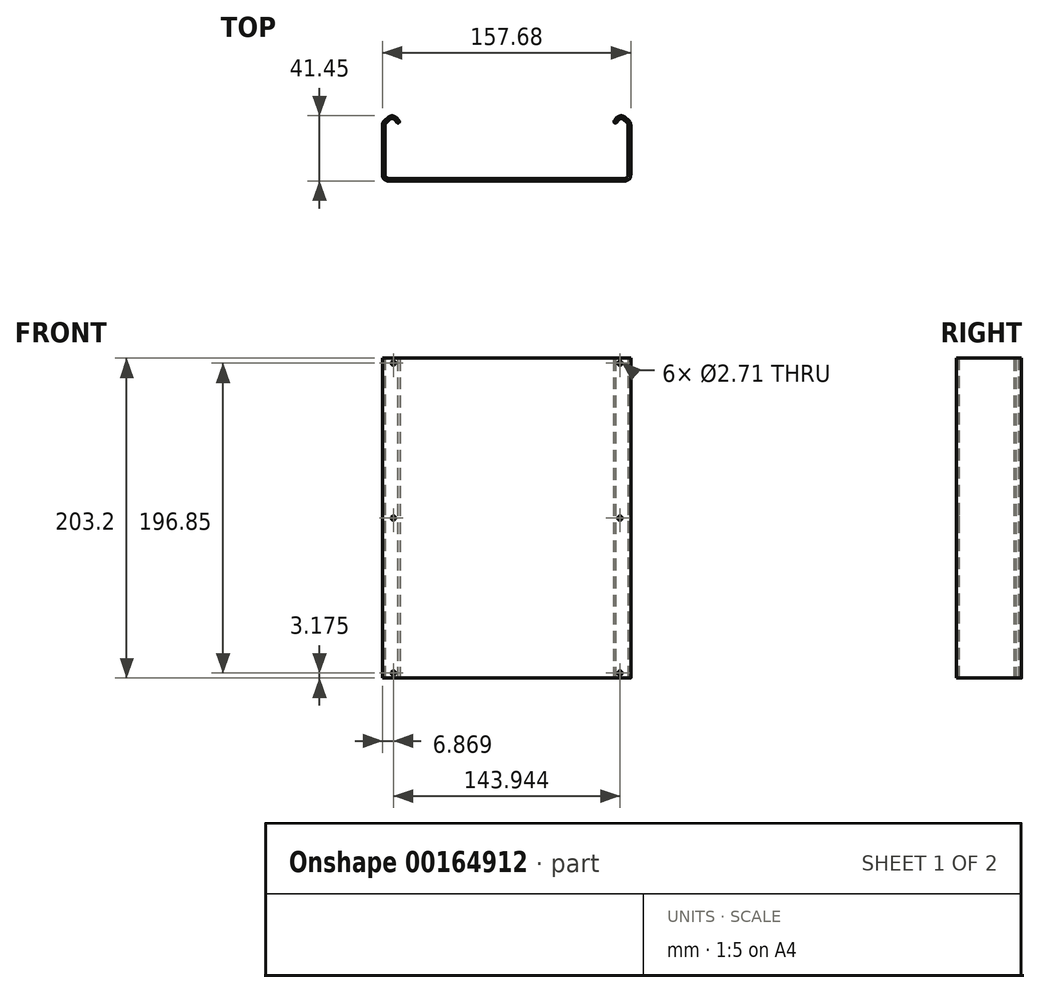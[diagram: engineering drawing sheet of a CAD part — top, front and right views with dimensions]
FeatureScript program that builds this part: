
annotation { "Feature Type Name" : "Feature", "Feature Type Description" : "" }
export const myFeature = defineFeature(function(context is Context, id is Id, definition is map)
    precondition{}
    {
        {
            var Q0;
            Q0=qCreatedBy(makeId("Top.planeOp"),FACE);
            var sketch = newSketch(context, id + "F0", { "sketchPlane" : qUnion([Q0])});
            skLineSegment(sketch, "E0", {"start": v(0, 0) * mm, "end": v(4.63, 3.93) * mm});
            skLineSegment(sketch, "E1", {"start": v(4.63, 3.93) * mm, "end": v(7.97, 0) * mm});
            skLineSegment(sketch, "E2", {"start": v(7.97, 0) * mm, "end": v(9.27, 1.1) * mm});
            skLineSegment(sketch, "E3", {"start": v(9.27, 1.1) * mm, "end": v(4.83, 6.34) * mm});
            skLineSegment(sketch, "E4", {"start": v(4.83, 6.34) * mm, "end": v(-1.7, 0.8) * mm});
            skLineSegment(sketch, "E5", {"start": v(0, 0) * mm, "end": v(0, -34.91) * mm});
            skLineSegment(sketch, "E6", {"start": v(0, -34.91) * mm, "end": v(154.26, -34.91) * mm});
            skLineSegment(sketch, "E7", {"start": v(155.97, -36.62) * mm, "end": v(-1.7, -36.62) * mm});
            skLineSegment(sketch, "E8", {"start": v(-1.7, -36.62) * mm, "end": v(-1.7, 0.8) * mm});
            skLineSegment(sketch, "E9", {"start": v(2.32, 1.97) * mm, "end": v(1.21, 3.27) * mm, "construction": true});
            skLineSegment(sketch, "E10", {"start": v(0, -34.91) * mm, "end": v(-1.7, -34.91) * mm, "construction": true});
            skLineSegment(sketch, "E11", {"start": v(77.13, -36.62) * mm, "end": v(77.13, -34.91) * mm, "construction": true});
            skLineSegment(sketch, "E12", {"start": v(154.26, -34.91) * mm, "end": v(154.26, 0) * mm});
            skLineSegment(sketch, "E13", {"start": v(154.26, 0) * mm, "end": v(149.63, 3.93) * mm});
            skLineSegment(sketch, "E14", {"start": v(149.63, 3.93) * mm, "end": v(146.29, 0) * mm});
            skLineSegment(sketch, "E15", {"start": v(146.29, 0) * mm, "end": v(144.99, 1.1) * mm});
            skLineSegment(sketch, "E16", {"start": v(144.99, 1.1) * mm, "end": v(149.43, 6.34) * mm});
            skLineSegment(sketch, "E17", {"start": v(149.43, 6.34) * mm, "end": v(155.97, 0.8) * mm});
            skLineSegment(sketch, "E18", {"start": v(155.97, 0.8) * mm, "end": v(155.97, -36.62) * mm});
            skArc(sketch, "E19", {"start": v(7.22, 3.53) * mm, "mid": v(4.7, 4.82) * mm, "end": v(2.01, 3.95) * mm, "construction": true});
            skArc(sketch, "E20", {"start": v(-0.4, 1.9) * mm, "mid": v(-1.37, 0.63) * mm, "end": v(-1.7, -0.92) * mm, "construction": true});
            skLineSegment(sketch, "E21", {"start": v(4.83, 6.34) * mm, "end": v(149.43, 6.34) * mm, "construction": true});
            skSolve(sketch);
        }
        {
            var Q0;
            Q0=qSketchRegion(id+"F0",true);
            extrude(context, id + "F1", {"entities" : qUnion([Q0]), "depth" : 203.2 * mm});
        }
        {
            var Q0;
            Q0=makeQuery(id+"F1.opExtrude","SWEPT_EDGE",EDGE,{"disambiguationData":[OSD([sQuery(id+"F0.wireOp",EDGE,"E16"),sQuery(id+"F0.wireOp",EDGE,"E17")])]});
            var Q1;
            Q1=makeQuery(id+"F1.opExtrude","SWEPT_EDGE",EDGE,{"disambiguationData":[OSD([sQuery(id+"F0.wireOp",EDGE,"E17"),sQuery(id+"F0.wireOp",EDGE,"E18")])]});
            var Q2;
            Q2=makeQuery(id+"F1.opExtrude","SWEPT_EDGE",EDGE,{"disambiguationData":[OSD([sQuery(id+"F0.wireOp",EDGE,"E7"),sQuery(id+"F0.wireOp",EDGE,"E18")])]});
            var Q3;
            Q3=makeQuery(id+"F1.opExtrude","SWEPT_EDGE",EDGE,{"disambiguationData":[OSD([sQuery(id+"F0.wireOp",EDGE,"E7"),sQuery(id+"F0.wireOp",EDGE,"E8")])]});
            var Q4;
            Q4=makeQuery(id+"F1.opExtrude","SWEPT_EDGE",EDGE,{"disambiguationData":[OSD([sQuery(id+"F0.wireOp",EDGE,"E4"),sQuery(id+"F0.wireOp",EDGE,"E8")])]});
            var Q5;
            Q5=makeQuery(id+"F1.opExtrude","SWEPT_EDGE",EDGE,{"disambiguationData":[OSD([sQuery(id+"F0.wireOp",EDGE,"E3"),sQuery(id+"F0.wireOp",EDGE,"E4")])]});
            fillet(context, id + "F2", {"entities" : qUnion([Q0, Q1, Q2, Q3, Q4, Q5]), "radius" : 3.7 * mm, "tangentPropagation" : true, "allowEdgeOverflow" : false});
        }
        {
            var Q0;
            Q0=makeQuery(id+"F1.opExtrude","SWEPT_EDGE",EDGE,{"disambiguationData":[OSD([sQuery(id+"F0.wireOp",EDGE,"E13"),sQuery(id+"F0.wireOp",EDGE,"E14")])]});
            var Q1;
            Q1=makeQuery(id+"F1.opExtrude","SWEPT_EDGE",EDGE,{"disambiguationData":[OSD([sQuery(id+"F0.wireOp",EDGE,"E12"),sQuery(id+"F0.wireOp",EDGE,"E13")])]});
            var Q2;
            Q2=makeQuery(id+"F1.opExtrude","SWEPT_EDGE",EDGE,{"disambiguationData":[OSD([sQuery(id+"F0.wireOp",EDGE,"E6"),sQuery(id+"F0.wireOp",EDGE,"E12")])]});
            var Q3;
            Q3=makeQuery(id+"F1.opExtrude","SWEPT_EDGE",EDGE,{"disambiguationData":[OSD([sQuery(id+"F0.wireOp",EDGE,"E5"),sQuery(id+"F0.wireOp",EDGE,"E6")])]});
            var Q4;
            Q4=makeQuery(id+"F1.opExtrude","SWEPT_EDGE",EDGE,{"disambiguationData":[OSD([sQuery(id+"F0.wireOp",EDGE,"E0"),sQuery(id+"F0.wireOp",EDGE,"E5")])]});
            var Q5;
            Q5=makeQuery(id+"F1.opExtrude","SWEPT_EDGE",EDGE,{"disambiguationData":[OSD([sQuery(id+"F0.wireOp",EDGE,"E0"),sQuery(id+"F0.wireOp",EDGE,"E1")])]});
            fillet(context, id + "F3", {"entities" : qUnion([Q0, Q1, Q2, Q3, Q4, Q5]), "radius" : 1.98 * mm, "tangentPropagation" : true, "allowEdgeOverflow" : false});
        }
        {
            var Q0;
            Q0=makeQuery(id+"F1.opExtrude","CAP_EDGE",EDGE,{"disambiguationData":[OSD([sQuery(id+"F0.wireOp",EDGE,"E15")])],"isStart":false});
            var Q1;
            Q1=makeQuery(id+"F1.opExtrude","CAP_EDGE",EDGE,{"disambiguationData":[OSD([sQuery(id+"F0.wireOp",EDGE,"E15")])],"isStart":true});
            var Q2;
            Q2=makeQuery(id+"F1.opExtrude","CAP_EDGE",EDGE,{"disambiguationData":[OSD([sQuery(id+"F0.wireOp",EDGE,"E2")])],"isStart":true});
            var Q3;
            Q3=makeQuery(id+"F1.opExtrude","CAP_EDGE",EDGE,{"disambiguationData":[OSD([sQuery(id+"F0.wireOp",EDGE,"E2")])],"isStart":false});
            fillet(context, id + "F4", {"entities" : qUnion([Q0, Q1, Q2, Q3]), "radius" : 0.76 * mm, "tangentPropagation" : true, "allowEdgeOverflow" : false});
        }
        {
            var Q0;
            Q0=makeQuery(id+"F1.opExtrude","SWEPT_FACE",FACE,{"disambiguationData":[OSD([sQuery(id+"F0.wireOp",EDGE,"E6")])]});
            var sketch = newSketch(context, id + "F5", { "sketchPlane" : qUnion([Q0])});
            skLineSegment(sketch, "E22.bottom", {"start": v(-1.98, 0) * mm, "end": v(-5.16, 0) * mm, "construction": true});
            skLineSegment(sketch, "E22.top", {"start": v(-1.98, 3.17) * mm, "end": v(-5.16, 3.17) * mm, "construction": true});
            skLineSegment(sketch, "E22.left", {"start": v(-1.98, 0) * mm, "end": v(-1.98, 3.17) * mm, "construction": true});
            skLineSegment(sketch, "E22.right", {"start": v(-5.16, 0) * mm, "end": v(-5.16, 3.18) * mm, "construction": true});
            skLineSegment(sketch, "E23", {"start": v(-77.13, 0) * mm, "end": v(-77.13, 203.2) * mm, "construction": true});
            skLineSegment(sketch, "E24.bottom", {"start": v(-5.16, 3.17) * mm, "end": v(-149.1, 3.17) * mm, "construction": true});
            skLineSegment(sketch, "E24.top", {"start": v(-5.16, 200.03) * mm, "end": v(-149.1, 200.03) * mm, "construction": true});
            skLineSegment(sketch, "E24.left", {"start": v(-5.16, 3.17) * mm, "end": v(-5.16, 200.03) * mm, "construction": true});
            skLineSegment(sketch, "E24.right", {"start": v(-149.1, 3.17) * mm, "end": v(-149.1, 200.03) * mm, "construction": true});
            skPoint(sketch, "E24.middle", {"position": v(-77.13, 101.6) * mm});
            skCircle(sketch, "E25", {"center": v(-5.16, 3.17) * mm, "radius": 1.35 * mm});
            skCircle(sketch, "E26", {"center": v(-5.16, 101.6) * mm, "radius": 1.35 * mm});
            skCircle(sketch, "E27", {"center": v(-5.16, 200.03) * mm, "radius": 1.35 * mm});
            skCircle(sketch, "E28", {"center": v(-149.1, 200.03) * mm, "radius": 1.35 * mm});
            skCircle(sketch, "E29", {"center": v(-149.1, 101.6) * mm, "radius": 1.35 * mm});
            skCircle(sketch, "E30", {"center": v(-149.1, 3.17) * mm, "radius": 1.35 * mm});
            skSolve(sketch);
        }
        {
            var Q0;
            Q0 = qSketchRegion(id + "F5", true);
            var Q1;
            Q1=makeQuery(id+"F1.opExtrude","SWEPT_FACE",FACE,{"disambiguationData":[OSD([sQuery(id+"F0.wireOp",EDGE,"E7")])]});
            extrude(context, id + "F6", {"entities" : qUnion([Q0]), "operationType" : NewBodyOperationType.REMOVE, "endBound" : BoundingType.UP_TO_SURFACE, "oppositeDirection" : true, "endBoundEntityFace" : qUnion([Q1]), "depth" : 25.4 * mm});
        }
    });
